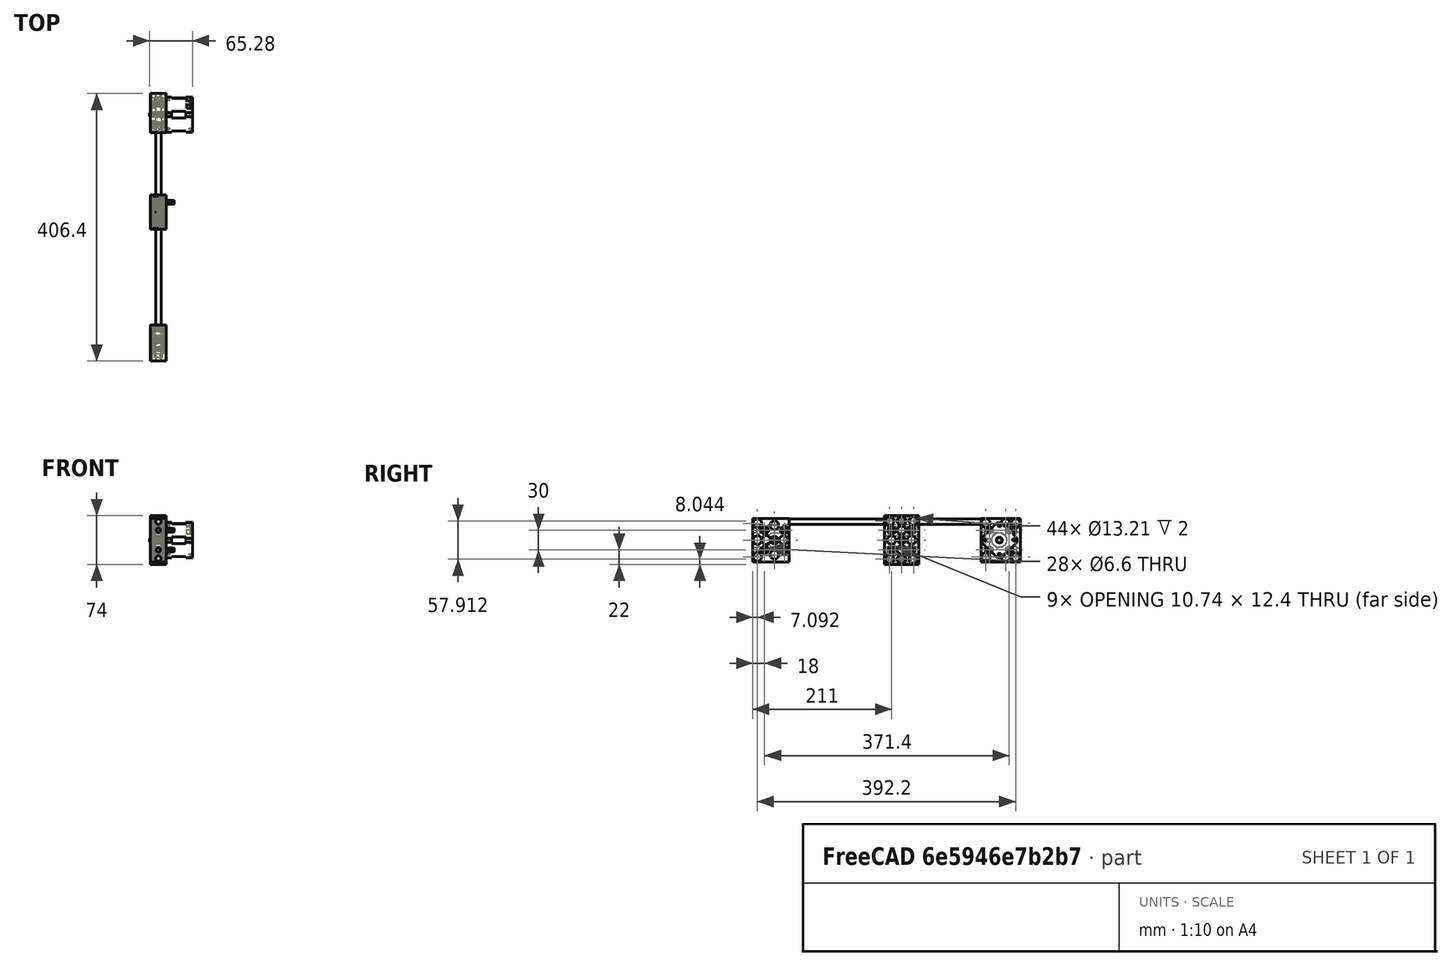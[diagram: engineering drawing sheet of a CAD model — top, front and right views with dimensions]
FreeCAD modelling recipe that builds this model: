
FCSTD DOCUMENT  (FreeCAD 0.16R6707 (Git))
Label: D3D Left Y Axis
License: CreativeCommons Attribution
LicenseURL: http://creativecommons.org/licenses/by/4.0/
objects: Part::FeaturePython×29, Part::Feature×9, App::FeaturePython×4, Part::Mirroring×3, Part::MultiFuse×3, Part::Cylinder×1, App::DocumentObjectGroup×1
note: 45 computed .brp shape members not serialized (recipe doc carries the construction recipe); baked Part::Feature solids carry a one-line shape summary decoded from their .brp

FEATURE [Part::FeaturePython] Universal_axis_idler_side_01  # a2plus imported part (geometry in sourceFile) (typed FeaturePython)
  Placement = pos=(0,0,0) rot=(0.57735,0.57735,0.57735;2.0944rad)
  fixedPosition = true
  sourceFile = <userpath>/Downloads/Freecad/D3D Printer/Universal_axis_idler_side.fcstd
  timeLastImport = 1.48765e+09
  updateColors = true
FEATURE [Part::Mirroring] Part__Mirroring  label="Universal_axis_idler_side_01 (Mirror #1)"
  Base = (0,0,0)
  Normal = (1,0,0)
  Source = -> Universal_axis_idler_side_01
FEATURE [Part::MultiFuse] Fusion  label="Y1 Universal Axis Idler"
  Placement = pos=(12,33,32.44) rot=(0,0,1;0rad)
  Shapes = -> [Part__Mirroring,Universal_axis_idler_side_01]
FEATURE [Part::Cylinder] Cylinder  label="Rod"
  Angle = 360
  Height = 406.4
  Placement = pos=(12,8.8212e-07,4.43996) rot=(0,0.707107,0.707107;3.14159rad)
  Radius = 3.96875
FEATURE [Part::FeaturePython] Clone006  label="Clone of Rod"  # Draft clone (typed FeaturePython)
  Objects = -> [Cylinder]
  Placement = pos=(11.9844,8.8212e-07,60.44) rot=(-1,0,0;1.5708rad)
  Scale = (1,1,1)
FEATURE [Part::Feature] Part__Feature  label="NEMA 17 Stepper Motor"
  Placement = pos=(63.878,374.398,32.4108) rot=(-0.678489,-0.281611,0.678489;2.59259rad)
  shape: bbox 65.28 x 53.47 x 53.47 mm, 77 faces (baked)
FEATURE [Part::FeaturePython] Universal_axis_motor_side_01  # a2plus imported part (geometry in sourceFile) (typed FeaturePython)
  fixedPosition = false
  sourceFile = <userpath>/Downloads/Freecad/D3D Printer/Universal_axis_motor_side.fcstd
  timeLastImport = 1.48765e+09
  updateColors = true
FEATURE [Part::Mirroring] Part__Mirroring003  label="Universal_axis_motor_side_01 (Mirror #3)"
  Base = (0,0,0)
  Normal = (0,0,1)
  Source = -> Universal_axis_motor_side_01
FEATURE [Part::MultiFuse] Fusion005  label="Y1 Universal Axis Motor"
  Placement = pos=(12,374.4,32.44) rot=(0.57735,-0.57735,-0.57735;2.0944rad)
  Shapes = -> [Part__Mirroring003,Universal_axis_motor_side_01]
FEATURE [App::FeaturePython] planeConstraint01  label="Rods"  # a2plus constraint (typed FeaturePython)
  Object1 = Fusion005
  Object2 = Cylinder
  SubElement1 = Face3
  SubElement2 = Face2
  Type = plane
  directionConstraint = 0
  offset = 0
FEATURE [App::FeaturePython] planeConstraint02  label="Rods / Axis Motor "  # a2plus constraint (typed FeaturePython)
  Object1 = Fusion005
  Object2 = Clone006
  SubElement1 = Face42
  SubElement2 = Face2
  Type = plane
  directionConstraint = 0
  offset = 0
FEATURE [App::FeaturePython] planeConstraint03  label="Rods / Axis Idler"  # a2plus constraint (typed FeaturePython)
  Object1 = Fusion
  Object2 = Cylinder
  SubElement1 = Face3
  SubElement2 = Face3
  Type = plane
  directionConstraint = 1
  offset = 0
FEATURE [Part::FeaturePython] carriage_8mm_rods_01  # a2plus imported part (geometry in sourceFile) (typed FeaturePython)
  Placement = pos=(12.5,0,0) rot=(0,0,1;0rad)
  fixedPosition = false
  sourceFile = <userpath>/Downloads/Freecad/D3D Printer/Mess Stuff/axis_8mm STL + FCSTD/carriage_8mm_rods.FCStd
  timeLastImport = 1.48802e+09
  updateColors = true
FEATURE [Part::Mirroring] Part__Mirroring004  label="carriage_8mm_rods_01 (Mirror #3)"
  Base = (0,0,0)
  Normal = (0,0,1)
  Source = -> carriage_8mm_rods_01
FEATURE [App::FeaturePython] planeConstraint04  label="NEMA / Axis Motor001"  # a2plus constraint (typed FeaturePython)
  Object1 = Part__Feature
  Object2 = Fusion005
  SubElement1 = Face51
  SubElement2 = Face1
  Type = plane
  directionConstraint = 1
  offset = 0
FEATURE [Part::FeaturePython] M6_16_socket_bolt01  # a2plus imported part (geometry in sourceFile) (typed FeaturePython)
  Placement = pos=(-1.05543e-06,48,17.44) rot=(0,-1,0;1.5708rad)
  fixedPosition = false
  sourceFile = <userpath>/Downloads/Freecad/D3D Printer/Mess Stuff/M6-16 socket bolt.STEP
  timeLastImport = 1.48801e+09
  updateColors = true
FEATURE [Part::FeaturePython] M6_16_socket_bolt02  # a2plus imported part (geometry in sourceFile) (typed FeaturePython)
  Placement = pos=(-1.05543e-06,18,17.44) rot=(0,-1,0;1.5708rad)
  fixedPosition = false
  sourceFile = <userpath>/Downloads/Freecad/D3D Printer/Mess Stuff/M6-16 socket bolt.STEP
  timeLastImport = 1.48801e+09
  updateColors = true
FEATURE [Part::FeaturePython] M6_16_socket_bolt03  # a2plus imported part (geometry in sourceFile) (typed FeaturePython)
  Placement = pos=(-5.9833e-07,33,32.44) rot=(0,-1,0;1.5708rad)
  fixedPosition = false
  sourceFile = <userpath>/Downloads/Freecad/D3D Printer/Mess Stuff/M6-16 socket bolt.STEP
  timeLastImport = 1.48801e+09
  updateColors = true
FEATURE [Part::FeaturePython] M6_16_socket_bolt04  # a2plus imported part (geometry in sourceFile) (typed FeaturePython)
  Placement = pos=(-1.41228e-07,18,47.44) rot=(0,-1,0;1.5708rad)
  fixedPosition = false
  sourceFile = <userpath>/Downloads/Freecad/D3D Printer/Mess Stuff/M6-16 socket bolt.STEP
  timeLastImport = 1.48801e+09
  updateColors = true
FEATURE [Part::FeaturePython] M6_16_socket_bolt05  # a2plus imported part (geometry in sourceFile) (typed FeaturePython)
  Placement = pos=(-1.41228e-07,48,47.44) rot=(0,-1,0;1.5708rad)
  fixedPosition = false
  sourceFile = <userpath>/Downloads/Freecad/D3D Printer/Mess Stuff/M6-16 socket bolt.STEP
  timeLastImport = 1.48801e+09
  updateColors = true
FEATURE [Part::FeaturePython] M6_16_socket_bolt11  # a2plus imported part (geometry in sourceFile) (typed FeaturePython)
  Placement = pos=(-1.41228e-07,389.4,47.44) rot=(0,-1,0;1.5708rad)
  fixedPosition = false
  sourceFile = <userpath>/Downloads/Freecad/D3D Printer/Mess Stuff/M6-16 socket bolt.STEP
  timeLastImport = 1.48801e+09
  updateColors = true
FEATURE [Part::FeaturePython] M6_16_socket_bolt12  # a2plus imported part (geometry in sourceFile) (typed FeaturePython)
  Placement = pos=(-1.41228e-07,359.4,47.44) rot=(0,-1,0;1.5708rad)
  fixedPosition = false
  sourceFile = <userpath>/Downloads/Freecad/D3D Printer/Mess Stuff/M6-16 socket bolt.STEP
  timeLastImport = 1.48801e+09
  updateColors = true
FEATURE [Part::FeaturePython] M6_16_socket_bolt13  # a2plus imported part (geometry in sourceFile) (typed FeaturePython)
  Placement = pos=(-1.05543e-06,389.4,17.44) rot=(0,-1,0;1.5708rad)
  fixedPosition = false
  sourceFile = <userpath>/Downloads/Freecad/D3D Printer/Mess Stuff/M6-16 socket bolt.STEP
  timeLastImport = 1.48801e+09
  updateColors = true
FEATURE [Part::FeaturePython] M6_16_socket_bolt14  # a2plus imported part (geometry in sourceFile) (typed FeaturePython)
  Placement = pos=(-1.05543e-06,359.4,17.44) rot=(0,-1,0;1.5708rad)
  fixedPosition = false
  sourceFile = <userpath>/Downloads/Freecad/D3D Printer/Mess Stuff/M6-16 socket bolt.STEP
  timeLastImport = 1.48801e+09
  updateColors = true
FEATURE [Part::FeaturePython] m6_nut01  # a2plus imported part (geometry in sourceFile) (typed FeaturePython)
  Placement = pos=(3.5,18,17.44) rot=(0,1,0;1.5708rad)
  fixedPosition = false
  sourceFile = <userpath>/Downloads/Freecad/D3D Printer/Mess Stuff/m6-nut.STEP
  timeLastImport = 1.48801e+09
  updateColors = true
FEATURE [Part::FeaturePython] m6_nut02  # a2plus imported part (geometry in sourceFile) (typed FeaturePython)
  Placement = pos=(3.5,48,17.44) rot=(0,1,0;1.5708rad)
  fixedPosition = false
  sourceFile = <userpath>/Downloads/Freecad/D3D Printer/Mess Stuff/m6-nut.STEP
  timeLastImport = 1.48801e+09
  updateColors = true
FEATURE [Part::FeaturePython] m6_nut03  # a2plus imported part (geometry in sourceFile) (typed FeaturePython)
  Placement = pos=(3.5,33,32.44) rot=(0,1,0;1.5708rad)
  fixedPosition = false
  sourceFile = <userpath>/Downloads/Freecad/D3D Printer/Mess Stuff/m6-nut.STEP
  timeLastImport = 1.48801e+09
  updateColors = true
FEATURE [Part::FeaturePython] m6_nut04  # a2plus imported part (geometry in sourceFile) (typed FeaturePython)
  Placement = pos=(3.5,18,47.44) rot=(0,1,0;1.5708rad)
  fixedPosition = false
  sourceFile = <userpath>/Downloads/Freecad/D3D Printer/Mess Stuff/m6-nut.STEP
  timeLastImport = 1.48801e+09
  updateColors = true
FEATURE [Part::FeaturePython] m6_nut05  # a2plus imported part (geometry in sourceFile) (typed FeaturePython)
  Placement = pos=(3.5,48,47.44) rot=(0,1,0;1.5708rad)
  fixedPosition = false
  sourceFile = <userpath>/Downloads/Freecad/D3D Printer/Mess Stuff/m6-nut.STEP
  timeLastImport = 1.48801e+09
  updateColors = true
FEATURE [Part::FeaturePython] m6_nut11  # a2plus imported part (geometry in sourceFile) (typed FeaturePython)
  Placement = pos=(3,210.992,17.4088) rot=(0.250563,0.935113,0.250563;1.63783rad)
  fixedPosition = false
  sourceFile = <userpath>/Downloads/Freecad/D3D Printer/Mess Stuff/m6-nut.STEP
  timeLastImport = 1.48801e+09
  updateColors = true
FEATURE [Part::Feature] Part__Feature001  label="Pulley"
  Placement = pos=(20.068,374.4,32.44) rot=(0.678598,-0.678598,0.281085;2.59356rad)
  shape: bbox 11 x 12.62 x 12.62 mm, 94 faces (baked)
FEATURE [Part::Feature] Part__Feature002  label="MK8"
  Placement = pos=(16.9019,376.706,30.2684) rot=(1,0,0;2.35619rad)
  shape: bbox 3 x 3.394 x 3.394 mm, 13 faces (baked)
FEATURE [Part::Feature] Part__Feature003  label="ball_bearing"
  Placement = pos=(14,33,32.44) rot=(0,-1,0;1.5708rad)
  shape: bbox 8 x 13.6 x 13.6 mm, 82 faces (baked)
FEATURE [Part::FeaturePython] M6_16_socket_bolt08  # a2plus imported part (geometry in sourceFile) (typed FeaturePython)
  Placement = pos=(-1.28431e-06,211,17.44) rot=(0,-1,0;1.5708rad)
  fixedPosition = false
  sourceFile = <userpath>/Downloads/Freecad/D3D Printer/Mess Stuff/M6-16 socket bolt.STEP
  timeLastImport = 1.48801e+09
  updateColors = true
FEATURE [Part::Feature] Part__Feature004  label="lmuu 8mm bearing"
  Placement = pos=(0,-28,0) rot=(0,0,1;1.5708rad)
  shape: bbox 24 x 15 x 15 mm, 38 faces (baked)
FEATURE [Part::FeaturePython] Clone  label="lmuu 8mm bearing001"  # Draft clone (typed FeaturePython)
  Objects = -> [Part__Feature004]
  Placement = pos=(25,-28,0) rot=(0,0,1;1.5708rad)
  Scale = (1,1,1)
FEATURE [Part::FeaturePython] Clone007  label="lmuu 8mm bearing002"  # Draft clone (typed FeaturePython)
  Objects = -> [Part__Feature004]
  Placement = pos=(0,28,0) rot=(0,0,1;1.5708rad)
  Scale = (1,1,1)
FEATURE [Part::FeaturePython] Clone008  label="lmuu 8mm bearing003"  # Draft clone (typed FeaturePython)
  Objects = -> [Clone007]
  Placement = pos=(25,28,0) rot=(0,0,1;1.5708rad)
  Scale = (1,1,1)
FEATURE [Part::MultiFuse] Fusion006  label="Y1 Universal Axis Carriage"
  Placement = pos=(11.9844,238.5,32.44) rot=(0.57735,-0.57735,-0.57735;2.0944rad)
  Shapes = -> [Part__Mirroring004,carriage_8mm_rods_01,Part__Feature004,Clone,Clone007,Clone008]
FEATURE [Part::FeaturePython] m6_nut06  # a2plus imported part (geometry in sourceFile) (typed FeaturePython)
  Placement = pos=(3.5,389.4,47.44) rot=(0.250563,0.935113,0.250563;1.63783rad)
  fixedPosition = false
  sourceFile = <userpath>/Downloads/Freecad/D3D Printer/Mess Stuff/m6-nut.STEP
  timeLastImport = 1.48801e+09
  updateColors = true
FEATURE [Part::FeaturePython] m6_nut07  # a2plus imported part (geometry in sourceFile) (typed FeaturePython)
  Placement = pos=(3.5,359.4,47.44) rot=(0.250563,0.935113,0.250563;1.63783rad)
  fixedPosition = false
  sourceFile = <userpath>/Downloads/Freecad/D3D Printer/Mess Stuff/m6-nut.STEP
  timeLastImport = 1.48801e+09
  updateColors = true
FEATURE [Part::FeaturePython] m6_nut08  # a2plus imported part (geometry in sourceFile) (typed FeaturePython)
  Placement = pos=(3.5,359.4,17.44) rot=(0.250563,0.935113,0.250563;1.63783rad)
  fixedPosition = false
  sourceFile = <userpath>/Downloads/Freecad/D3D Printer/Mess Stuff/m6-nut.STEP
  timeLastImport = 1.48801e+09
  updateColors = true
FEATURE [Part::FeaturePython] m6_nut09  # a2plus imported part (geometry in sourceFile) (typed FeaturePython)
  Placement = pos=(3.5,389.4,17.44) rot=(0.250563,0.935113,0.250563;1.63783rad)
  fixedPosition = false
  sourceFile = <userpath>/Downloads/Freecad/D3D Printer/Mess Stuff/m6-nut.STEP
  timeLastImport = 1.48801e+09
  updateColors = true
FEATURE [Part::Feature] m6_nut  label="m6_nut016"
  Placement = pos=(3,226.018,32.4303) rot=(0.250563,0.935113,0.250563;1.63783rad)
  shape: bbox 5.626 x 11.55 x 11.55 mm, 49 faces (baked)
FEATURE [Part::Feature] m6_nut015  label="m6_nut017"
  Placement = pos=(3,210.986,47.4379) rot=(0.250563,0.935113,0.250563;1.63783rad)
  shape: bbox 5.626 x 11.55 x 11.55 mm, 49 faces (baked)
FEATURE [App::DocumentObjectGroup] Group  label="nuts bolts"
  Group = -> [M6_16_socket_bolt01,M6_16_socket_bolt02,M6_16_socket_bolt03,M6_16_socket_bolt04,M6_16_socket_bolt05,M6_16_socket_bolt11,M6_16_socket_bolt12,M6_16_socket_bolt13,M6_16_socket_bolt14,m6_nut01,m6_nut02,m6_nut03,m6_nut04,m6_nut05,m6_nut11,M6_16_socket_bolt08,m6_nut06,m6_nut07,m6_nut08,m6_nut09,m6_nut,m6_nut015]
FEATURE [Part::FeaturePython] Clone009  label="Clone of M6_16_socket_bolt08"  # Draft clone (typed FeaturePython)
  Objects = -> [M6_16_socket_bolt08]
  Placement = pos=(-3.70108e-07,211,47.44) rot=(0,-1,0;1.5708rad)
  Scale = (1,1,1)
FEATURE [Part::FeaturePython] Clone010  label="Clone of M6_16_socket_bolt009"  # Draft clone (typed FeaturePython)
  Objects = -> [M6_16_socket_bolt08]
  Placement = pos=(-8.2721e-07,226,32.44) rot=(0,-1,0;1.5708rad)
  Scale = (1,1,1)
FEATURE [Part::Feature] Part__Feature006  label="M6x30"
  Placement = pos=(35.9844,241.06,47.3656) rot=(0,1,0;1.5708rad)
  shape: bbox 36.21 x 10 x 10 mm, 148 faces (baked)
FEATURE [Part::Feature] Part__Feature007  label="M6x30 001"
  Placement = pos=(35.9844,241,17.44) rot=(0,1,0;1.5708rad)
  shape: bbox 36.21 x 10 x 10 mm, 148 faces (baked)
